# Revit family: 3D BIM Model HydroWELL Select 20, 30 and 50
name_source: partatom
category: Generic Models
units: mm (PartAtom-declared; Revit-internal decimal feet)

## family parameters
Always vertical = No
Can host rebar = No
Cut with Voids When Loaded = No
Part Type = Normal
Room Calculation Point = No
Round Connector Dimension = Use Radius
Shared = No
Work Plane-Based = No

## types (3) — shared parameters
Body = Aluminum 1100-H14
Description = Ultra Violet Disinfection
Manufacturer = Hydrotec
URL = http://www.hydrotec.co.uk

## per-type parameters (varying)
| type | Discharge offset | E/2 | FLG | Flange Connection | Flow Rate | Mass | Model | R |
| Select 20 | 80 mm  [stored 0.262467 ft] | 50 mm  [stored 0.164042 ft] | 100 mm  [stored 0.328084 ft] | 100 mm  [stored 0.328084 ft] | 7.1 L/s | 50.00 kg | HydroPUR Select 20
HydroPUR Select 20 | 50 mm  [stored 0.164042 ft] |
| Select 30 | 80 mm  [stored 0.262467 ft] | 50 mm  [stored 0.164042 ft] | 100 mm  [stored 0.328084 ft] | 100 mm  [stored 0.328084 ft] | 12.8 L/s | 60.00 kg | HydroPUR Select 30
HydroPUR Select 20 | 50 mm  [stored 0.164042 ft] |
| Select 50 | 105 mm | 75 mm | 125 mm | 150 mm | 18.5 L/s | 70.00 kg | HydroPUR Select 50
HydroPUR Select 20 | 75 mm |

note: [stored X ft] marks values corroborated as IEEE doubles in the binary element streams (Revit-internal decimal feet)

## geometry (parser evidence)
native form markers: Sweep x9
no freeform markers — native parametric forms only
